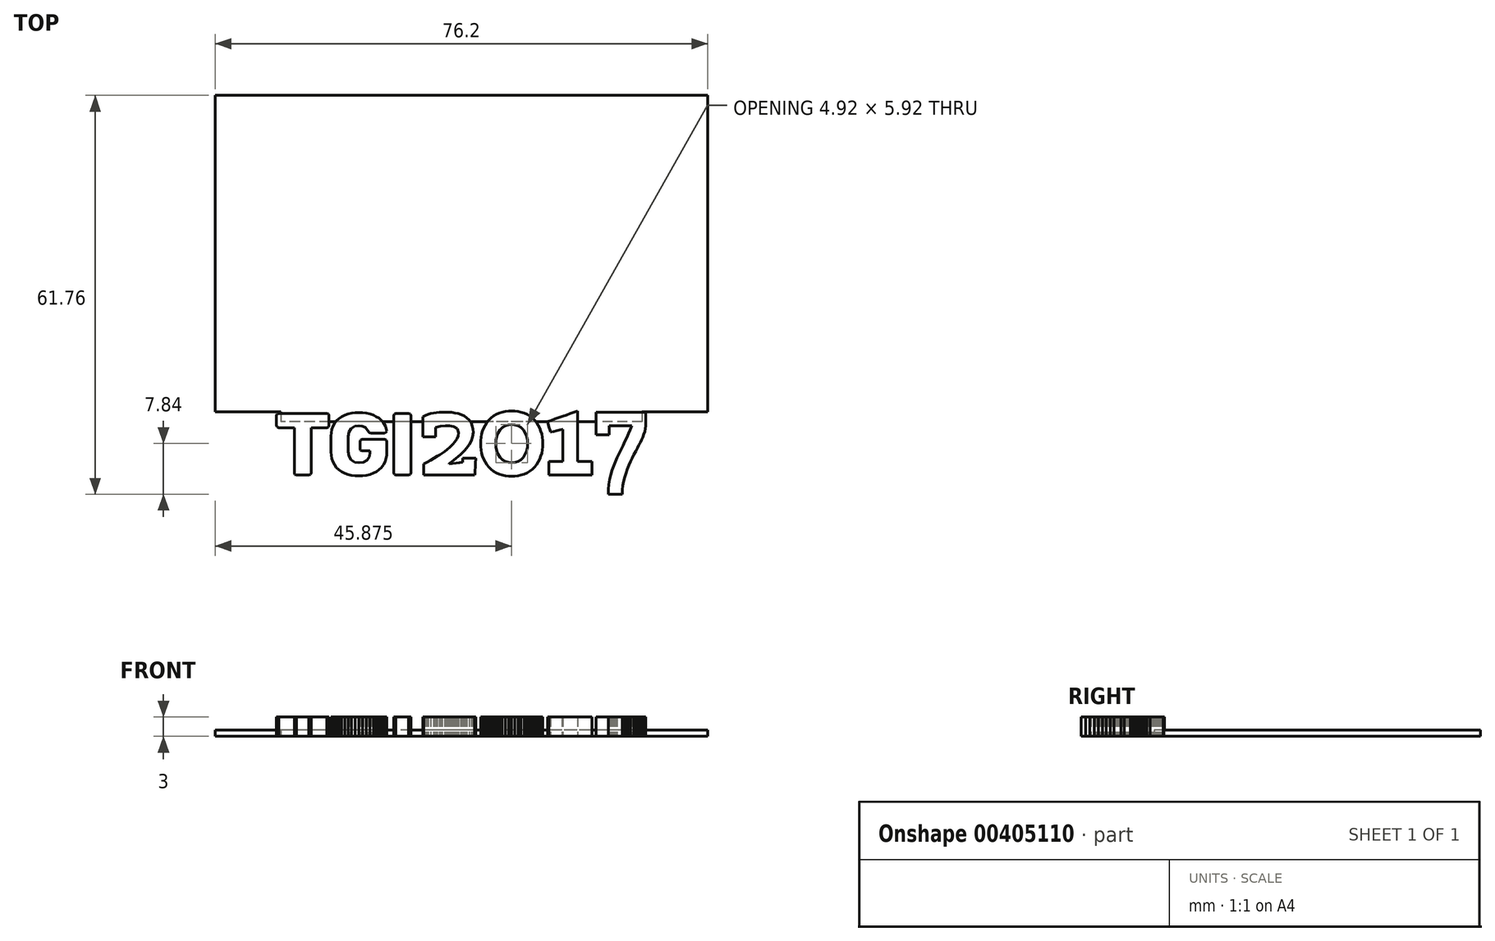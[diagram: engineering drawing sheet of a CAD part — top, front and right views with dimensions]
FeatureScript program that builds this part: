
annotation { "Feature Type Name" : "Feature", "Feature Type Description" : "" }
export const myFeature = defineFeature(function(context is Context, id is Id, definition is map)
    precondition{}
    {
        {
            var Q0;
            Q0=qCreatedBy(makeId("Top.planeOp"),FACE);
            var sketch = newSketch(context, id + "F0", { "sketchPlane" : qUnion([Q0])});
            skLineSegment(sketch, "E0.bottom", {"start": v(38.1, 24.5) * mm, "end": v(-38.1, 24.5) * mm});
            skLineSegment(sketch, "E0.top", {"start": v(38.1, -24.5) * mm, "end": v(-38.1, -24.5) * mm});
            skLineSegment(sketch, "E0.left", {"start": v(38.1, 24.5) * mm, "end": v(38.1, -24.5) * mm});
            skLineSegment(sketch, "E0.right", {"start": v(-38.1, 24.5) * mm, "end": v(-38.1, -24.5) * mm});
            skPoint(sketch, "E0.middle", {"position": v(0, 0) * mm});
            skPoint(sketch, "E1.middle", {"position": v(0, -24.5) * mm});
            skLineSegment(sketch, "E2.bottom", {"start": v(27.94, -23) * mm, "end": v(-27.94, -23) * mm});
            skLineSegment(sketch, "E2.top", {"start": v(27.94, -26) * mm, "end": v(-27.94, -26) * mm});
            skLineSegment(sketch, "E2.left", {"start": v(27.94, -23) * mm, "end": v(27.94, -26) * mm});
            skLineSegment(sketch, "E2.right", {"start": v(-27.94, -23) * mm, "end": v(-27.94, -26) * mm});
            skSolve(sketch);
        }
        {
            var Q0;
            Q0=makeQuery(id+"F0.imprint","IMPRINT",FACE,{"disambiguationData":[TD([[makeQuery(id+"F0.imprint","IMPRINT",EDGE,{"derivedFrom":sQuery(id+"F0.wireOp",EDGE,"E0.bottom")}),1.0]])]});
            var Q1;
            {var subQ5=sQuery(id+"F0.wireOp",EDGE,"E2.bottom");Q1=makeQuery(id+"F0.imprint","IMPRINT",FACE,{"disambiguationData":[TD([[makeQuery(id+"F0.imprint","IMPRINT",EDGE,{"derivedFrom":subQ5}),1.0]])]});}
            var Q2;
            {var subQ5=sQuery(id+"F0.wireOp",EDGE,"E2.top");Q2=makeQuery(id+"F0.imprint","IMPRINT",FACE,{"disambiguationData":[TD([[makeQuery(id+"F0.imprint","IMPRINT",EDGE,{"derivedFrom":subQ5}),-1.0]])]});}
            extrude(context, id + "F1", {"entities" : qUnion([Q0, Q1, Q2]), "depth" : 1 * mm});
        }
        {
            var Q0;
            Q0=qCreatedBy(makeId("Top.planeOp"),FACE);
            var sketch = newSketch(context, id + "F2", { "sketchPlane" : qUnion([Q0])});
            skLineSegment(sketch, "E3", {"start": v(-25.76, -34.2) * mm, "end": v(-25.86, -33.96) * mm});
            skLineSegment(sketch, "E4", {"start": v(-25.86, -33.96) * mm, "end": v(-25.86, -33.77) * mm});
            skLineSegment(sketch, "E5", {"start": v(-25.86, -33.77) * mm, "end": v(-25.86, -33.26) * mm});
            skLineSegment(sketch, "E6", {"start": v(-25.86, -33.26) * mm, "end": v(-25.86, -32.56) * mm});
            skLineSegment(sketch, "E7", {"start": v(-25.86, -32.56) * mm, "end": v(-25.86, -31.86) * mm});
            skLineSegment(sketch, "E8", {"start": v(-25.86, -31.86) * mm, "end": v(-25.86, -31.16) * mm});
            skLineSegment(sketch, "E9", {"start": v(-25.86, -31.16) * mm, "end": v(-25.86, -30.46) * mm});
            skLineSegment(sketch, "E10", {"start": v(-25.86, -30.46) * mm, "end": v(-25.86, -29.76) * mm});
            skLineSegment(sketch, "E11", {"start": v(-25.86, -29.76) * mm, "end": v(-25.86, -29.06) * mm});
            skLineSegment(sketch, "E12", {"start": v(-25.86, -29.06) * mm, "end": v(-25.86, -28.37) * mm});
            skLineSegment(sketch, "E13", {"start": v(-25.86, -28.37) * mm, "end": v(-25.86, -27.67) * mm});
            skLineSegment(sketch, "E14", {"start": v(-25.86, -27.67) * mm, "end": v(-25.86, -27.16) * mm});
            skLineSegment(sketch, "E15", {"start": v(-25.86, -27.16) * mm, "end": v(-25.86, -26.97) * mm});
            skLineSegment(sketch, "E16", {"start": v(-25.86, -26.97) * mm, "end": v(-26.03, -26.97) * mm});
            skLineSegment(sketch, "E17", {"start": v(-26.03, -26.97) * mm, "end": v(-26.46, -26.97) * mm});
            skLineSegment(sketch, "E18", {"start": v(-26.46, -26.97) * mm, "end": v(-27.06, -26.97) * mm});
            skLineSegment(sketch, "E19", {"start": v(-27.06, -26.97) * mm, "end": v(-27.66, -26.97) * mm});
            skLineSegment(sketch, "E20", {"start": v(-27.66, -26.97) * mm, "end": v(-28.1, -26.97) * mm});
            skLineSegment(sketch, "E21", {"start": v(-28.1, -26.97) * mm, "end": v(-28.26, -26.97) * mm});
            skLineSegment(sketch, "E22", {"start": v(-28.26, -26.97) * mm, "end": v(-28.52, -26.87) * mm});
            skLineSegment(sketch, "E23", {"start": v(-28.52, -26.87) * mm, "end": v(-28.62, -26.63) * mm});
            skLineSegment(sketch, "E24", {"start": v(-28.62, -26.63) * mm, "end": v(-28.62, -26.39) * mm});
            skLineSegment(sketch, "E25", {"start": v(-28.62, -26.39) * mm, "end": v(-28.62, -25.86) * mm});
            skLineSegment(sketch, "E26", {"start": v(-28.62, -25.86) * mm, "end": v(-28.62, -25.34) * mm});
            skLineSegment(sketch, "E27", {"start": v(-28.62, -25.34) * mm, "end": v(-28.62, -25.1) * mm});
            skLineSegment(sketch, "E28", {"start": v(-28.62, -25.1) * mm, "end": v(-28.52, -24.85) * mm});
            skLineSegment(sketch, "E29", {"start": v(-28.52, -24.85) * mm, "end": v(-28.26, -24.74) * mm});
            skLineSegment(sketch, "E30", {"start": v(-28.26, -24.74) * mm, "end": v(-27.65, -24.74) * mm});
            skLineSegment(sketch, "E31", {"start": v(-27.65, -24.74) * mm, "end": v(-27.03, -24.74) * mm});
            skLineSegment(sketch, "E32", {"start": v(-27.03, -24.74) * mm, "end": v(-26.41, -24.74) * mm});
            skLineSegment(sketch, "E33", {"start": v(-26.41, -24.74) * mm, "end": v(-25.8, -24.74) * mm});
            skLineSegment(sketch, "E34", {"start": v(-25.8, -24.74) * mm, "end": v(-25.18, -24.74) * mm});
            skLineSegment(sketch, "E35", {"start": v(-25.18, -24.74) * mm, "end": v(-24.56, -24.74) * mm});
            skLineSegment(sketch, "E36", {"start": v(-24.56, -24.74) * mm, "end": v(-23.94, -24.74) * mm});
            skLineSegment(sketch, "E37", {"start": v(-23.94, -24.74) * mm, "end": v(-23.32, -24.74) * mm});
            skLineSegment(sketch, "E38", {"start": v(-23.32, -24.74) * mm, "end": v(-22.7, -24.74) * mm});
            skLineSegment(sketch, "E39", {"start": v(-22.7, -24.74) * mm, "end": v(-22.09, -24.74) * mm});
            skLineSegment(sketch, "E40", {"start": v(-22.09, -24.74) * mm, "end": v(-21.47, -24.74) * mm});
            skLineSegment(sketch, "E41", {"start": v(-21.47, -24.74) * mm, "end": v(-20.85, -24.74) * mm});
            skLineSegment(sketch, "E42", {"start": v(-20.85, -24.74) * mm, "end": v(-20.6, -24.85) * mm});
            skLineSegment(sketch, "E43", {"start": v(-20.6, -24.85) * mm, "end": v(-20.5, -25.1) * mm});
            skLineSegment(sketch, "E44", {"start": v(-20.5, -25.1) * mm, "end": v(-20.5, -25.34) * mm});
            skLineSegment(sketch, "E45", {"start": v(-20.5, -25.34) * mm, "end": v(-20.5, -25.86) * mm});
            skLineSegment(sketch, "E46", {"start": v(-20.5, -25.86) * mm, "end": v(-20.5, -26.39) * mm});
            skLineSegment(sketch, "E47", {"start": v(-20.5, -26.39) * mm, "end": v(-20.5, -26.63) * mm});
            skLineSegment(sketch, "E48", {"start": v(-20.5, -26.63) * mm, "end": v(-20.6, -26.87) * mm});
            skLineSegment(sketch, "E49", {"start": v(-20.6, -26.87) * mm, "end": v(-20.85, -26.97) * mm});
            skLineSegment(sketch, "E50", {"start": v(-20.85, -26.97) * mm, "end": v(-21.02, -26.97) * mm});
            skLineSegment(sketch, "E51", {"start": v(-21.02, -26.97) * mm, "end": v(-21.45, -26.97) * mm});
            skLineSegment(sketch, "E52", {"start": v(-21.45, -26.97) * mm, "end": v(-22.05, -26.97) * mm});
            skLineSegment(sketch, "E53", {"start": v(-22.05, -26.97) * mm, "end": v(-22.65, -26.97) * mm});
            skLineSegment(sketch, "E54", {"start": v(-22.65, -26.97) * mm, "end": v(-23.08, -26.97) * mm});
            skLineSegment(sketch, "E55", {"start": v(-23.08, -26.97) * mm, "end": v(-23.25, -26.97) * mm});
            skLineSegment(sketch, "E56", {"start": v(-23.25, -26.97) * mm, "end": v(-23.25, -27.16) * mm});
            skLineSegment(sketch, "E57", {"start": v(-23.25, -27.16) * mm, "end": v(-23.25, -27.67) * mm});
            skLineSegment(sketch, "E58", {"start": v(-23.25, -27.67) * mm, "end": v(-23.25, -28.37) * mm});
            skLineSegment(sketch, "E59", {"start": v(-23.25, -28.37) * mm, "end": v(-23.25, -29.06) * mm});
            skLineSegment(sketch, "E60", {"start": v(-23.25, -29.06) * mm, "end": v(-23.25, -29.76) * mm});
            skLineSegment(sketch, "E61", {"start": v(-23.25, -29.76) * mm, "end": v(-23.25, -30.46) * mm});
            skLineSegment(sketch, "E62", {"start": v(-23.25, -30.46) * mm, "end": v(-23.25, -31.16) * mm});
            skLineSegment(sketch, "E63", {"start": v(-23.25, -31.16) * mm, "end": v(-23.25, -31.86) * mm});
            skLineSegment(sketch, "E64", {"start": v(-23.25, -31.86) * mm, "end": v(-23.25, -32.56) * mm});
            skLineSegment(sketch, "E65", {"start": v(-23.25, -32.56) * mm, "end": v(-23.25, -33.26) * mm});
            skLineSegment(sketch, "E66", {"start": v(-23.25, -33.26) * mm, "end": v(-23.25, -33.77) * mm});
            skLineSegment(sketch, "E67", {"start": v(-23.25, -33.77) * mm, "end": v(-23.25, -33.96) * mm});
            skLineSegment(sketch, "E68", {"start": v(-23.25, -33.96) * mm, "end": v(-23.36, -34.2) * mm});
            skLineSegment(sketch, "E69", {"start": v(-23.36, -34.2) * mm, "end": v(-23.6, -34.3) * mm});
            skLineSegment(sketch, "E70", {"start": v(-23.6, -34.3) * mm, "end": v(-24.08, -34.3) * mm});
            skLineSegment(sketch, "E71", {"start": v(-24.08, -34.3) * mm, "end": v(-24.56, -34.3) * mm});
            skLineSegment(sketch, "E72", {"start": v(-24.56, -34.3) * mm, "end": v(-25.03, -34.3) * mm});
            skLineSegment(sketch, "E73", {"start": v(-25.03, -34.3) * mm, "end": v(-25.5, -34.3) * mm});
            skLineSegment(sketch, "E74", {"start": v(-25.5, -34.3) * mm, "end": v(-25.76, -34.2) * mm});
            skLineSegment(sketch, "E75", {"start": v(-18.99, -33.47) * mm, "end": v(-19.35, -33.1) * mm});
            skLineSegment(sketch, "E76", {"start": v(-19.35, -33.1) * mm, "end": v(-19.65, -32.69) * mm});
            skLineSegment(sketch, "E77", {"start": v(-19.65, -32.69) * mm, "end": v(-19.87, -32.23) * mm});
            skLineSegment(sketch, "E78", {"start": v(-19.87, -32.23) * mm, "end": v(-20.03, -31.74) * mm});
            skLineSegment(sketch, "E79", {"start": v(-20.03, -31.74) * mm, "end": v(-20.13, -31.24) * mm});
            skLineSegment(sketch, "E80", {"start": v(-20.13, -31.24) * mm, "end": v(-20.17, -30.72) * mm});
            skLineSegment(sketch, "E81", {"start": v(-20.17, -30.72) * mm, "end": v(-20.19, -30.1) * mm});
            skLineSegment(sketch, "E82", {"start": v(-20.19, -30.1) * mm, "end": v(-20.19, -29.48) * mm});
            skLineSegment(sketch, "E83", {"start": v(-20.19, -29.48) * mm, "end": v(-20.19, -28.85) * mm});
            skLineSegment(sketch, "E84", {"start": v(-20.19, -28.85) * mm, "end": v(-20.17, -28.22) * mm});
            skLineSegment(sketch, "E85", {"start": v(-20.17, -28.22) * mm, "end": v(-20.13, -27.72) * mm});
            skLineSegment(sketch, "E86", {"start": v(-20.13, -27.72) * mm, "end": v(-20.04, -27.23) * mm});
            skLineSegment(sketch, "E87", {"start": v(-20.04, -27.23) * mm, "end": v(-19.87, -26.75) * mm});
            skLineSegment(sketch, "E88", {"start": v(-19.87, -26.75) * mm, "end": v(-19.64, -26.3) * mm});
            skLineSegment(sketch, "E89", {"start": v(-19.64, -26.3) * mm, "end": v(-19.34, -25.9) * mm});
            skLineSegment(sketch, "E90", {"start": v(-19.34, -25.9) * mm, "end": v(-18.98, -25.56) * mm});
            skLineSegment(sketch, "E91", {"start": v(-18.98, -25.56) * mm, "end": v(-18.53, -25.24) * mm});
            skLineSegment(sketch, "E92", {"start": v(-18.53, -25.24) * mm, "end": v(-18.04, -25) * mm});
            skLineSegment(sketch, "E93", {"start": v(-18.04, -25) * mm, "end": v(-17.52, -24.8) * mm});
            skLineSegment(sketch, "E94", {"start": v(-17.52, -24.8) * mm, "end": v(-16.98, -24.7) * mm});
            skLineSegment(sketch, "E95", {"start": v(-16.98, -24.7) * mm, "end": v(-16.44, -24.63) * mm});
            skLineSegment(sketch, "E96", {"start": v(-16.44, -24.63) * mm, "end": v(-15.89, -24.6) * mm});
            skLineSegment(sketch, "E97", {"start": v(-15.89, -24.6) * mm, "end": v(-15.3, -24.63) * mm});
            skLineSegment(sketch, "E98", {"start": v(-15.3, -24.63) * mm, "end": v(-14.72, -24.7) * mm});
            skLineSegment(sketch, "E99", {"start": v(-14.72, -24.7) * mm, "end": v(-14.15, -24.83) * mm});
            skLineSegment(sketch, "E100", {"start": v(-14.15, -24.83) * mm, "end": v(-13.6, -25.03) * mm});
            skLineSegment(sketch, "E101", {"start": v(-13.6, -25.03) * mm, "end": v(-13.18, -25.23) * mm});
            skLineSegment(sketch, "E102", {"start": v(-13.18, -25.23) * mm, "end": v(-12.79, -25.48) * mm});
            skLineSegment(sketch, "E103", {"start": v(-12.79, -25.48) * mm, "end": v(-12.43, -25.77) * mm});
            skLineSegment(sketch, "E104", {"start": v(-12.43, -25.77) * mm, "end": v(-12.11, -26.12) * mm});
            skLineSegment(sketch, "E105", {"start": v(-12.11, -26.12) * mm, "end": v(-11.74, -26.75) * mm});
            skLineSegment(sketch, "E106", {"start": v(-11.74, -26.75) * mm, "end": v(-11.57, -27.47) * mm});
            skLineSegment(sketch, "E107", {"start": v(-11.57, -27.47) * mm, "end": v(-11.66, -27.69) * mm});
            skLineSegment(sketch, "E108", {"start": v(-11.66, -27.69) * mm, "end": v(-11.87, -27.77) * mm});
            skLineSegment(sketch, "E109", {"start": v(-11.87, -27.77) * mm, "end": v(-12.4, -27.77) * mm});
            skLineSegment(sketch, "E110", {"start": v(-12.4, -27.77) * mm, "end": v(-12.93, -27.77) * mm});
            skLineSegment(sketch, "E111", {"start": v(-12.93, -27.77) * mm, "end": v(-13.46, -27.77) * mm});
            skLineSegment(sketch, "E112", {"start": v(-13.46, -27.77) * mm, "end": v(-14, -27.77) * mm});
            skLineSegment(sketch, "E113", {"start": v(-14, -27.77) * mm, "end": v(-14.2, -27.73) * mm});
            skLineSegment(sketch, "E114", {"start": v(-14.2, -27.73) * mm, "end": v(-14.34, -27.58) * mm});
            skLineSegment(sketch, "E115", {"start": v(-14.34, -27.58) * mm, "end": v(-14.87, -26.93) * mm});
            skLineSegment(sketch, "E116", {"start": v(-14.87, -26.93) * mm, "end": v(-15.36, -26.7) * mm});
            skLineSegment(sketch, "E117", {"start": v(-15.36, -26.7) * mm, "end": v(-15.89, -26.65) * mm});
            skLineSegment(sketch, "E118", {"start": v(-15.89, -26.65) * mm, "end": v(-16.54, -26.74) * mm});
            skLineSegment(sketch, "E119", {"start": v(-16.54, -26.74) * mm, "end": v(-17.1, -27.08) * mm});
            skLineSegment(sketch, "E120", {"start": v(-17.1, -27.08) * mm, "end": v(-17.43, -27.64) * mm});
            skLineSegment(sketch, "E121", {"start": v(-17.43, -27.64) * mm, "end": v(-17.53, -28.3) * mm});
            skLineSegment(sketch, "E122", {"start": v(-17.53, -28.3) * mm, "end": v(-17.54, -28.88) * mm});
            skLineSegment(sketch, "E123", {"start": v(-17.54, -28.88) * mm, "end": v(-17.54, -29.47) * mm});
            skLineSegment(sketch, "E124", {"start": v(-17.54, -29.47) * mm, "end": v(-17.54, -30.06) * mm});
            skLineSegment(sketch, "E125", {"start": v(-17.54, -30.06) * mm, "end": v(-17.53, -30.65) * mm});
            skLineSegment(sketch, "E126", {"start": v(-17.53, -30.65) * mm, "end": v(-17.43, -31.33) * mm});
            skLineSegment(sketch, "E127", {"start": v(-17.43, -31.33) * mm, "end": v(-17.1, -31.93) * mm});
            skLineSegment(sketch, "E128", {"start": v(-17.1, -31.93) * mm, "end": v(-16.54, -32.3) * mm});
            skLineSegment(sketch, "E129", {"start": v(-16.54, -32.3) * mm, "end": v(-15.86, -32.39) * mm});
            skLineSegment(sketch, "E130", {"start": v(-15.86, -32.39) * mm, "end": v(-15.2, -32.3) * mm});
            skLineSegment(sketch, "E131", {"start": v(-15.2, -32.3) * mm, "end": v(-14.6, -32) * mm});
            skLineSegment(sketch, "E132", {"start": v(-14.6, -32) * mm, "end": v(-14.24, -31.45) * mm});
            skLineSegment(sketch, "E133", {"start": v(-14.24, -31.45) * mm, "end": v(-14.14, -30.8) * mm});
            skLineSegment(sketch, "E134", {"start": v(-14.14, -30.8) * mm, "end": v(-14.14, -30.67) * mm});
            skLineSegment(sketch, "E135", {"start": v(-14.14, -30.67) * mm, "end": v(-14.14, -30.54) * mm});
            skLineSegment(sketch, "E136", {"start": v(-14.14, -30.54) * mm, "end": v(-14.33, -30.54) * mm});
            skLineSegment(sketch, "E137", {"start": v(-14.33, -30.54) * mm, "end": v(-14.75, -30.54) * mm});
            skLineSegment(sketch, "E138", {"start": v(-14.75, -30.54) * mm, "end": v(-15.17, -30.54) * mm});
            skLineSegment(sketch, "E139", {"start": v(-15.17, -30.54) * mm, "end": v(-15.36, -30.54) * mm});
            skLineSegment(sketch, "E140", {"start": v(-15.36, -30.54) * mm, "end": v(-15.6, -30.44) * mm});
            skLineSegment(sketch, "E141", {"start": v(-15.6, -30.44) * mm, "end": v(-15.71, -30.2) * mm});
            skLineSegment(sketch, "E142", {"start": v(-15.71, -30.2) * mm, "end": v(-15.71, -30.02) * mm});
            skLineSegment(sketch, "E143", {"start": v(-15.71, -30.02) * mm, "end": v(-15.71, -29.66) * mm});
            skLineSegment(sketch, "E144", {"start": v(-15.71, -29.66) * mm, "end": v(-15.71, -29.3) * mm});
            skLineSegment(sketch, "E145", {"start": v(-15.71, -29.3) * mm, "end": v(-15.71, -29.13) * mm});
            skLineSegment(sketch, "E146", {"start": v(-15.71, -29.13) * mm, "end": v(-15.6, -28.87) * mm});
            skLineSegment(sketch, "E147", {"start": v(-15.6, -28.87) * mm, "end": v(-15.36, -28.77) * mm});
            skLineSegment(sketch, "E148", {"start": v(-15.36, -28.77) * mm, "end": v(-14.78, -28.77) * mm});
            skLineSegment(sketch, "E149", {"start": v(-14.78, -28.77) * mm, "end": v(-14.2, -28.77) * mm});
            skLineSegment(sketch, "E150", {"start": v(-14.2, -28.77) * mm, "end": v(-13.62, -28.77) * mm});
            skLineSegment(sketch, "E151", {"start": v(-13.62, -28.77) * mm, "end": v(-13.04, -28.77) * mm});
            skLineSegment(sketch, "E152", {"start": v(-13.04, -28.77) * mm, "end": v(-12.47, -28.77) * mm});
            skLineSegment(sketch, "E153", {"start": v(-12.47, -28.77) * mm, "end": v(-11.89, -28.77) * mm});
            skLineSegment(sketch, "E154", {"start": v(-11.89, -28.77) * mm, "end": v(-11.64, -28.87) * mm});
            skLineSegment(sketch, "E155", {"start": v(-11.64, -28.87) * mm, "end": v(-11.53, -29.13) * mm});
            skLineSegment(sketch, "E156", {"start": v(-11.53, -29.13) * mm, "end": v(-11.53, -29.37) * mm});
            skLineSegment(sketch, "E157", {"start": v(-11.53, -29.37) * mm, "end": v(-11.53, -29.92) * mm});
            skLineSegment(sketch, "E158", {"start": v(-11.53, -29.92) * mm, "end": v(-11.53, -30.46) * mm});
            skLineSegment(sketch, "E159", {"start": v(-11.53, -30.46) * mm, "end": v(-11.53, -30.7) * mm});
            skLineSegment(sketch, "E160", {"start": v(-11.53, -30.7) * mm, "end": v(-11.56, -31.23) * mm});
            skLineSegment(sketch, "E161", {"start": v(-11.56, -31.23) * mm, "end": v(-11.66, -31.75) * mm});
            skLineSegment(sketch, "E162", {"start": v(-11.66, -31.75) * mm, "end": v(-11.83, -32.25) * mm});
            skLineSegment(sketch, "E163", {"start": v(-11.83, -32.25) * mm, "end": v(-12.07, -32.7) * mm});
            skLineSegment(sketch, "E164", {"start": v(-12.07, -32.7) * mm, "end": v(-12.38, -33.11) * mm});
            skLineSegment(sketch, "E165", {"start": v(-12.38, -33.11) * mm, "end": v(-12.74, -33.46) * mm});
            skLineSegment(sketch, "E166", {"start": v(-12.74, -33.46) * mm, "end": v(-13.15, -33.76) * mm});
            skLineSegment(sketch, "E167", {"start": v(-13.15, -33.76) * mm, "end": v(-13.6, -34) * mm});
            skLineSegment(sketch, "E168", {"start": v(-13.6, -34) * mm, "end": v(-14.14, -34.2) * mm});
            skLineSegment(sketch, "E169", {"start": v(-14.14, -34.2) * mm, "end": v(-14.72, -34.34) * mm});
            skLineSegment(sketch, "E170", {"start": v(-14.72, -34.34) * mm, "end": v(-15.3, -34.41) * mm});
            skLineSegment(sketch, "E171", {"start": v(-15.3, -34.41) * mm, "end": v(-15.89, -34.44) * mm});
            skLineSegment(sketch, "E172", {"start": v(-15.89, -34.44) * mm, "end": v(-16.44, -34.42) * mm});
            skLineSegment(sketch, "E173", {"start": v(-16.44, -34.42) * mm, "end": v(-16.99, -34.35) * mm});
            skLineSegment(sketch, "E174", {"start": v(-16.99, -34.35) * mm, "end": v(-17.53, -34.23) * mm});
            skLineSegment(sketch, "E175", {"start": v(-17.53, -34.23) * mm, "end": v(-18.05, -34.05) * mm});
            skLineSegment(sketch, "E176", {"start": v(-18.05, -34.05) * mm, "end": v(-18.54, -33.8) * mm});
            skLineSegment(sketch, "E177", {"start": v(-18.54, -33.8) * mm, "end": v(-18.99, -33.47) * mm});
            skLineSegment(sketch, "E178", {"start": v(-10.37, -34.2) * mm, "end": v(-10.47, -33.96) * mm});
            skLineSegment(sketch, "E179", {"start": v(-10.47, -33.96) * mm, "end": v(-10.47, -33.8) * mm});
            skLineSegment(sketch, "E180", {"start": v(-10.47, -33.8) * mm, "end": v(-10.47, -33.32) * mm});
            skLineSegment(sketch, "E181", {"start": v(-10.47, -33.32) * mm, "end": v(-10.47, -32.7) * mm});
            skLineSegment(sketch, "E182", {"start": v(-10.47, -32.7) * mm, "end": v(-10.47, -32.06) * mm});
            skLineSegment(sketch, "E183", {"start": v(-10.47, -32.06) * mm, "end": v(-10.47, -31.42) * mm});
            skLineSegment(sketch, "E184", {"start": v(-10.47, -31.42) * mm, "end": v(-10.47, -30.79) * mm});
            skLineSegment(sketch, "E185", {"start": v(-10.47, -30.79) * mm, "end": v(-10.47, -30.15) * mm});
            skLineSegment(sketch, "E186", {"start": v(-10.47, -30.15) * mm, "end": v(-10.47, -29.52) * mm});
            skLineSegment(sketch, "E187", {"start": v(-10.47, -29.52) * mm, "end": v(-10.47, -28.89) * mm});
            skLineSegment(sketch, "E188", {"start": v(-10.47, -28.89) * mm, "end": v(-10.47, -28.25) * mm});
            skLineSegment(sketch, "E189", {"start": v(-10.47, -28.25) * mm, "end": v(-10.47, -27.62) * mm});
            skLineSegment(sketch, "E190", {"start": v(-10.47, -27.62) * mm, "end": v(-10.47, -26.99) * mm});
            skLineSegment(sketch, "E191", {"start": v(-10.47, -26.99) * mm, "end": v(-10.47, -26.35) * mm});
            skLineSegment(sketch, "E192", {"start": v(-10.47, -26.35) * mm, "end": v(-10.47, -25.72) * mm});
            skLineSegment(sketch, "E193", {"start": v(-10.47, -25.72) * mm, "end": v(-10.47, -25.25) * mm});
            skLineSegment(sketch, "E194", {"start": v(-10.47, -25.25) * mm, "end": v(-10.47, -25.09) * mm});
            skLineSegment(sketch, "E195", {"start": v(-10.47, -25.09) * mm, "end": v(-10.37, -24.84) * mm});
            skLineSegment(sketch, "E196", {"start": v(-10.37, -24.84) * mm, "end": v(-10.13, -24.74) * mm});
            skLineSegment(sketch, "E197", {"start": v(-10.13, -24.74) * mm, "end": v(-9.64, -24.74) * mm});
            skLineSegment(sketch, "E198", {"start": v(-9.64, -24.74) * mm, "end": v(-9.15, -24.74) * mm});
            skLineSegment(sketch, "E199", {"start": v(-9.15, -24.74) * mm, "end": v(-8.67, -24.74) * mm});
            skLineSegment(sketch, "E200", {"start": v(-8.67, -24.74) * mm, "end": v(-8.18, -24.74) * mm});
            skLineSegment(sketch, "E201", {"start": v(-8.18, -24.74) * mm, "end": v(-7.93, -24.84) * mm});
            skLineSegment(sketch, "E202", {"start": v(-7.93, -24.84) * mm, "end": v(-7.84, -25.09) * mm});
            skLineSegment(sketch, "E203", {"start": v(-7.84, -25.09) * mm, "end": v(-7.84, -25.25) * mm});
            skLineSegment(sketch, "E204", {"start": v(-7.84, -25.25) * mm, "end": v(-7.84, -25.72) * mm});
            skLineSegment(sketch, "E205", {"start": v(-7.84, -25.72) * mm, "end": v(-7.84, -26.35) * mm});
            skLineSegment(sketch, "E206", {"start": v(-7.84, -26.35) * mm, "end": v(-7.84, -26.99) * mm});
            skLineSegment(sketch, "E207", {"start": v(-7.84, -26.99) * mm, "end": v(-7.84, -27.62) * mm});
            skLineSegment(sketch, "E208", {"start": v(-7.84, -27.62) * mm, "end": v(-7.84, -28.25) * mm});
            skLineSegment(sketch, "E209", {"start": v(-7.84, -28.25) * mm, "end": v(-7.84, -28.89) * mm});
            skLineSegment(sketch, "E210", {"start": v(-7.84, -28.89) * mm, "end": v(-7.84, -29.52) * mm});
            skLineSegment(sketch, "E211", {"start": v(-7.84, -29.52) * mm, "end": v(-7.84, -30.15) * mm});
            skLineSegment(sketch, "E212", {"start": v(-7.84, -30.15) * mm, "end": v(-7.84, -30.79) * mm});
            skLineSegment(sketch, "E213", {"start": v(-7.84, -30.79) * mm, "end": v(-7.84, -31.42) * mm});
            skLineSegment(sketch, "E214", {"start": v(-7.84, -31.42) * mm, "end": v(-7.84, -32.06) * mm});
            skLineSegment(sketch, "E215", {"start": v(-7.84, -32.06) * mm, "end": v(-7.84, -32.7) * mm});
            skLineSegment(sketch, "E216", {"start": v(-7.84, -32.7) * mm, "end": v(-7.84, -33.32) * mm});
            skLineSegment(sketch, "E217", {"start": v(-7.84, -33.32) * mm, "end": v(-7.84, -33.8) * mm});
            skLineSegment(sketch, "E218", {"start": v(-7.84, -33.8) * mm, "end": v(-7.84, -33.96) * mm});
            skLineSegment(sketch, "E219", {"start": v(-7.84, -33.96) * mm, "end": v(-7.93, -34.2) * mm});
            skLineSegment(sketch, "E220", {"start": v(-7.93, -34.2) * mm, "end": v(-8.18, -34.3) * mm});
            skLineSegment(sketch, "E221", {"start": v(-8.18, -34.3) * mm, "end": v(-8.67, -34.3) * mm});
            skLineSegment(sketch, "E222", {"start": v(-8.67, -34.3) * mm, "end": v(-9.15, -34.3) * mm});
            skLineSegment(sketch, "E223", {"start": v(-9.15, -34.3) * mm, "end": v(-9.64, -34.3) * mm});
            skLineSegment(sketch, "E224", {"start": v(-9.64, -34.3) * mm, "end": v(-10.13, -34.3) * mm});
            skLineSegment(sketch, "E225", {"start": v(-10.13, -34.3) * mm, "end": v(-10.37, -34.2) * mm});
            skLineSegment(sketch, "E226", {"start": v(-5.85, -34.3) * mm, "end": v(-5.85, -34.03) * mm});
            skLineSegment(sketch, "E227", {"start": v(-5.85, -34.03) * mm, "end": v(-5.85, -33.43) * mm});
            skLineSegment(sketch, "E228", {"start": v(-5.85, -33.43) * mm, "end": v(-5.85, -32.83) * mm});
            skLineSegment(sketch, "E229", {"start": v(-5.85, -32.83) * mm, "end": v(-5.85, -32.56) * mm});
            skLineSegment(sketch, "E230", {"start": v(-5.85, -32.56) * mm, "end": v(-5.32, -32.28) * mm});
            skLineSegment(sketch, "E231", {"start": v(-5.32, -32.28) * mm, "end": v(-4.79, -32) * mm});
            skLineSegment(sketch, "E232", {"start": v(-4.79, -32) * mm, "end": v(-4.27, -31.7) * mm});
            skLineSegment(sketch, "E233", {"start": v(-4.27, -31.7) * mm, "end": v(-3.75, -31.38) * mm});
            skLineSegment(sketch, "E234", {"start": v(-3.75, -31.38) * mm, "end": v(-3.37, -31.14) * mm});
            skLineSegment(sketch, "E235", {"start": v(-3.37, -31.14) * mm, "end": v(-2.98, -30.89) * mm});
            skLineSegment(sketch, "E236", {"start": v(-2.98, -30.89) * mm, "end": v(-2.6, -30.63) * mm});
            skLineSegment(sketch, "E237", {"start": v(-2.6, -30.63) * mm, "end": v(-2.25, -30.35) * mm});
            skLineSegment(sketch, "E238", {"start": v(-2.25, -30.35) * mm, "end": v(-1.8, -29.96) * mm});
            skLineSegment(sketch, "E239", {"start": v(-1.8, -29.96) * mm, "end": v(-1.36, -29.54) * mm});
            skLineSegment(sketch, "E240", {"start": v(-1.36, -29.54) * mm, "end": v(-1, -29.15) * mm});
            skLineSegment(sketch, "E241", {"start": v(-1, -29.15) * mm, "end": v(-0.7, -28.72) * mm});
            skLineSegment(sketch, "E242", {"start": v(-0.7, -28.72) * mm, "end": v(-0.5, -28.23) * mm});
            skLineSegment(sketch, "E243", {"start": v(-0.5, -28.23) * mm, "end": v(-0.43, -27.71) * mm});
            skLineSegment(sketch, "E244", {"start": v(-0.43, -27.71) * mm, "end": v(-0.65, -27.12) * mm});
            skLineSegment(sketch, "E245", {"start": v(-0.65, -27.12) * mm, "end": v(-1.2, -26.8) * mm});
            skLineSegment(sketch, "E246", {"start": v(-1.2, -26.8) * mm, "end": v(-1.83, -26.66) * mm});
            skLineSegment(sketch, "E247", {"start": v(-1.83, -26.66) * mm, "end": v(-2.47, -26.63) * mm});
            skLineSegment(sketch, "E248", {"start": v(-2.47, -26.63) * mm, "end": v(-3.24, -26.7) * mm});
            skLineSegment(sketch, "E249", {"start": v(-3.24, -26.7) * mm, "end": v(-3.97, -26.93) * mm});
            skLineSegment(sketch, "E250", {"start": v(-3.97, -26.93) * mm, "end": v(-3.97, -27.15) * mm});
            skLineSegment(sketch, "E251", {"start": v(-3.97, -27.15) * mm, "end": v(-3.97, -27.65) * mm});
            skLineSegment(sketch, "E252", {"start": v(-3.97, -27.65) * mm, "end": v(-3.97, -28.15) * mm});
            skLineSegment(sketch, "E253", {"start": v(-3.97, -28.15) * mm, "end": v(-3.97, -28.37) * mm});
            skLineSegment(sketch, "E254", {"start": v(-3.97, -28.37) * mm, "end": v(-4.47, -28.37) * mm});
            skLineSegment(sketch, "E255", {"start": v(-4.47, -28.37) * mm, "end": v(-4.97, -28.37) * mm});
            skLineSegment(sketch, "E256", {"start": v(-4.97, -28.37) * mm, "end": v(-5.47, -28.37) * mm});
            skLineSegment(sketch, "E257", {"start": v(-5.47, -28.37) * mm, "end": v(-5.97, -28.37) * mm});
            skLineSegment(sketch, "E258", {"start": v(-5.97, -28.37) * mm, "end": v(-5.97, -28.15) * mm});
            skLineSegment(sketch, "E259", {"start": v(-5.97, -28.15) * mm, "end": v(-5.97, -27.6) * mm});
            skLineSegment(sketch, "E260", {"start": v(-5.97, -27.6) * mm, "end": v(-5.97, -26.81) * mm});
            skLineSegment(sketch, "E261", {"start": v(-5.97, -26.81) * mm, "end": v(-5.97, -26.03) * mm});
            skLineSegment(sketch, "E262", {"start": v(-5.97, -26.03) * mm, "end": v(-5.97, -25.48) * mm});
            skLineSegment(sketch, "E263", {"start": v(-5.97, -25.48) * mm, "end": v(-5.97, -25.25) * mm});
            skLineSegment(sketch, "E264", {"start": v(-5.97, -25.25) * mm, "end": v(-5.57, -25.06) * mm});
            skLineSegment(sketch, "E265", {"start": v(-5.57, -25.06) * mm, "end": v(-5.16, -24.9) * mm});
            skLineSegment(sketch, "E266", {"start": v(-5.16, -24.9) * mm, "end": v(-4.73, -24.78) * mm});
            skLineSegment(sketch, "E267", {"start": v(-4.73, -24.78) * mm, "end": v(-4.3, -24.69) * mm});
            skLineSegment(sketch, "E268", {"start": v(-4.3, -24.69) * mm, "end": v(-3.85, -24.62) * mm});
            skLineSegment(sketch, "E269", {"start": v(-3.85, -24.62) * mm, "end": v(-3.41, -24.57) * mm});
            skLineSegment(sketch, "E270", {"start": v(-3.41, -24.57) * mm, "end": v(-2.97, -24.55) * mm});
            skLineSegment(sketch, "E271", {"start": v(-2.97, -24.55) * mm, "end": v(-2.52, -24.54) * mm});
            skLineSegment(sketch, "E272", {"start": v(-2.52, -24.54) * mm, "end": v(-2.02, -24.55) * mm});
            skLineSegment(sketch, "E273", {"start": v(-2.02, -24.55) * mm, "end": v(-1.5, -24.59) * mm});
            skLineSegment(sketch, "E274", {"start": v(-1.5, -24.59) * mm, "end": v(-1, -24.66) * mm});
            skLineSegment(sketch, "E275", {"start": v(-1, -24.66) * mm, "end": v(-0.5, -24.77) * mm});
            skLineSegment(sketch, "E276", {"start": v(-0.5, -24.77) * mm, "end": v(-0.02, -24.93) * mm});
            skLineSegment(sketch, "E277", {"start": v(-0.02, -24.93) * mm, "end": v(0.44, -25.14) * mm});
            skLineSegment(sketch, "E278", {"start": v(0.44, -25.14) * mm, "end": v(0.86, -25.43) * mm});
            skLineSegment(sketch, "E279", {"start": v(0.86, -25.43) * mm, "end": v(1.22, -25.79) * mm});
            skLineSegment(sketch, "E280", {"start": v(1.22, -25.79) * mm, "end": v(1.5, -26.22) * mm});
            skLineSegment(sketch, "E281", {"start": v(1.5, -26.22) * mm, "end": v(1.68, -26.69) * mm});
            skLineSegment(sketch, "E282", {"start": v(1.68, -26.69) * mm, "end": v(1.78, -27.19) * mm});
            skLineSegment(sketch, "E283", {"start": v(1.78, -27.19) * mm, "end": v(1.81, -27.7) * mm});
            skLineSegment(sketch, "E284", {"start": v(1.81, -27.7) * mm, "end": v(1.73, -28.37) * mm});
            skLineSegment(sketch, "E285", {"start": v(1.73, -28.37) * mm, "end": v(1.51, -29) * mm});
            skLineSegment(sketch, "E286", {"start": v(1.51, -29) * mm, "end": v(1.18, -29.6) * mm});
            skLineSegment(sketch, "E287", {"start": v(1.18, -29.6) * mm, "end": v(0.78, -30.15) * mm});
            skLineSegment(sketch, "E288", {"start": v(0.78, -30.15) * mm, "end": v(0.48, -30.49) * mm});
            skLineSegment(sketch, "E289", {"start": v(0.48, -30.49) * mm, "end": v(0.18, -30.81) * mm});
            skLineSegment(sketch, "E290", {"start": v(0.18, -30.81) * mm, "end": v(-0.15, -31.12) * mm});
            skLineSegment(sketch, "E291", {"start": v(-0.15, -31.12) * mm, "end": v(-0.48, -31.42) * mm});
            skLineSegment(sketch, "E292", {"start": v(-0.48, -31.42) * mm, "end": v(-0.82, -31.7) * mm});
            skLineSegment(sketch, "E293", {"start": v(-0.82, -31.7) * mm, "end": v(-1.18, -31.98) * mm});
            skLineSegment(sketch, "E294", {"start": v(-1.18, -31.98) * mm, "end": v(-1.54, -32.24) * mm});
            skLineSegment(sketch, "E295", {"start": v(-1.54, -32.24) * mm, "end": v(-1.91, -32.49) * mm});
            skLineSegment(sketch, "E296", {"start": v(-1.91, -32.49) * mm, "end": v(-1.88, -32.54) * mm});
            skLineSegment(sketch, "E297", {"start": v(-1.88, -32.54) * mm, "end": v(-1.73, -32.52) * mm});
            skLineSegment(sketch, "E298", {"start": v(-1.73, -32.52) * mm, "end": v(-1.36, -32.48) * mm});
            skLineSegment(sketch, "E299", {"start": v(-1.36, -32.48) * mm, "end": v(-0.85, -32.42) * mm});
            skLineSegment(sketch, "E300", {"start": v(-0.85, -32.42) * mm, "end": v(-0.34, -32.36) * mm});
            skLineSegment(sketch, "E301", {"start": v(-0.34, -32.36) * mm, "end": v(0.03, -32.31) * mm});
            skLineSegment(sketch, "E302", {"start": v(0.03, -32.31) * mm, "end": v(0.18, -32.3) * mm});
            skLineSegment(sketch, "E303", {"start": v(0.18, -32.3) * mm, "end": v(0.2, -31.99) * mm});
            skLineSegment(sketch, "E304", {"start": v(0.2, -31.99) * mm, "end": v(0.21, -31.68) * mm});
            skLineSegment(sketch, "E305", {"start": v(0.21, -31.68) * mm, "end": v(0.71, -31.68) * mm});
            skLineSegment(sketch, "E306", {"start": v(0.71, -31.68) * mm, "end": v(1.21, -31.68) * mm});
            skLineSegment(sketch, "E307", {"start": v(1.21, -31.68) * mm, "end": v(1.72, -31.68) * mm});
            skLineSegment(sketch, "E308", {"start": v(1.72, -31.68) * mm, "end": v(2.22, -31.68) * mm});
            skLineSegment(sketch, "E309", {"start": v(2.22, -31.68) * mm, "end": v(2.2, -31.87) * mm});
            skLineSegment(sketch, "E310", {"start": v(2.2, -31.87) * mm, "end": v(2.18, -32.34) * mm});
            skLineSegment(sketch, "E311", {"start": v(2.18, -32.34) * mm, "end": v(2.14, -33) * mm});
            skLineSegment(sketch, "E312", {"start": v(2.14, -33) * mm, "end": v(2.1, -33.65) * mm});
            skLineSegment(sketch, "E313", {"start": v(2.1, -33.65) * mm, "end": v(2.07, -34.11) * mm});
            skLineSegment(sketch, "E314", {"start": v(2.07, -34.11) * mm, "end": v(2.06, -34.3) * mm});
            skLineSegment(sketch, "E315", {"start": v(2.06, -34.3) * mm, "end": v(1.88, -34.3) * mm});
            skLineSegment(sketch, "E316", {"start": v(1.88, -34.3) * mm, "end": v(1.4, -34.3) * mm});
            skLineSegment(sketch, "E317", {"start": v(1.4, -34.3) * mm, "end": v(0.74, -34.3) * mm});
            skLineSegment(sketch, "E318", {"start": v(0.74, -34.3) * mm, "end": v(0.08, -34.3) * mm});
            skLineSegment(sketch, "E319", {"start": v(0.08, -34.3) * mm, "end": v(-0.58, -34.3) * mm});
            skLineSegment(sketch, "E320", {"start": v(-0.58, -34.3) * mm, "end": v(-1.24, -34.3) * mm});
            skLineSegment(sketch, "E321", {"start": v(-1.24, -34.3) * mm, "end": v(-1.9, -34.3) * mm});
            skLineSegment(sketch, "E322", {"start": v(-1.9, -34.3) * mm, "end": v(-2.56, -34.3) * mm});
            skLineSegment(sketch, "E323", {"start": v(-2.56, -34.3) * mm, "end": v(-3.22, -34.3) * mm});
            skLineSegment(sketch, "E324", {"start": v(-3.22, -34.3) * mm, "end": v(-3.87, -34.3) * mm});
            skLineSegment(sketch, "E325", {"start": v(-3.87, -34.3) * mm, "end": v(-4.53, -34.3) * mm});
            skLineSegment(sketch, "E326", {"start": v(-4.53, -34.3) * mm, "end": v(-5.2, -34.3) * mm});
            skLineSegment(sketch, "E327", {"start": v(-5.2, -34.3) * mm, "end": v(-5.68, -34.3) * mm});
            skLineSegment(sketch, "E328", {"start": v(-5.68, -34.3) * mm, "end": v(-5.85, -34.3) * mm});
            skLineSegment(sketch, "E329", {"start": v(5.32, -29.42) * mm, "end": v(5.35, -29.99) * mm});
            skLineSegment(sketch, "E330", {"start": v(5.35, -29.99) * mm, "end": v(5.47, -30.54) * mm});
            skLineSegment(sketch, "E331", {"start": v(5.47, -30.54) * mm, "end": v(5.68, -31.07) * mm});
            skLineSegment(sketch, "E332", {"start": v(5.68, -31.07) * mm, "end": v(5.99, -31.55) * mm});
            skLineSegment(sketch, "E333", {"start": v(5.99, -31.55) * mm, "end": v(6.35, -31.9) * mm});
            skLineSegment(sketch, "E334", {"start": v(6.35, -31.9) * mm, "end": v(6.78, -32.18) * mm});
            skLineSegment(sketch, "E335", {"start": v(6.78, -32.18) * mm, "end": v(7.27, -32.34) * mm});
            skLineSegment(sketch, "E336", {"start": v(7.27, -32.34) * mm, "end": v(7.78, -32.38) * mm});
            skLineSegment(sketch, "E337", {"start": v(7.78, -32.38) * mm, "end": v(8.3, -32.34) * mm});
            skLineSegment(sketch, "E338", {"start": v(8.3, -32.34) * mm, "end": v(8.78, -32.18) * mm});
            skLineSegment(sketch, "E339", {"start": v(8.78, -32.18) * mm, "end": v(9.21, -31.9) * mm});
            skLineSegment(sketch, "E340", {"start": v(9.21, -31.9) * mm, "end": v(9.57, -31.55) * mm});
            skLineSegment(sketch, "E341", {"start": v(9.57, -31.55) * mm, "end": v(9.88, -31.07) * mm});
            skLineSegment(sketch, "E342", {"start": v(9.88, -31.07) * mm, "end": v(10.08, -30.54) * mm});
            skLineSegment(sketch, "E343", {"start": v(10.08, -30.54) * mm, "end": v(10.2, -29.99) * mm});
            skLineSegment(sketch, "E344", {"start": v(10.2, -29.99) * mm, "end": v(10.23, -29.42) * mm});
            skLineSegment(sketch, "E345", {"start": v(10.23, -29.42) * mm, "end": v(10.2, -28.85) * mm});
            skLineSegment(sketch, "E346", {"start": v(10.2, -28.85) * mm, "end": v(10.08, -28.3) * mm});
            skLineSegment(sketch, "E347", {"start": v(10.08, -28.3) * mm, "end": v(9.87, -27.77) * mm});
            skLineSegment(sketch, "E348", {"start": v(9.87, -27.77) * mm, "end": v(9.56, -27.3) * mm});
            skLineSegment(sketch, "E349", {"start": v(9.56, -27.3) * mm, "end": v(9.2, -26.93) * mm});
            skLineSegment(sketch, "E350", {"start": v(9.2, -26.93) * mm, "end": v(8.77, -26.66) * mm});
            skLineSegment(sketch, "E351", {"start": v(8.77, -26.66) * mm, "end": v(8.28, -26.5) * mm});
            skLineSegment(sketch, "E352", {"start": v(8.28, -26.5) * mm, "end": v(7.77, -26.46) * mm});
            skLineSegment(sketch, "E353", {"start": v(7.77, -26.46) * mm, "end": v(7.26, -26.5) * mm});
            skLineSegment(sketch, "E354", {"start": v(7.26, -26.5) * mm, "end": v(6.77, -26.66) * mm});
            skLineSegment(sketch, "E355", {"start": v(6.77, -26.66) * mm, "end": v(6.34, -26.93) * mm});
            skLineSegment(sketch, "E356", {"start": v(6.34, -26.93) * mm, "end": v(5.98, -27.3) * mm});
            skLineSegment(sketch, "E357", {"start": v(5.98, -27.3) * mm, "end": v(5.67, -27.77) * mm});
            skLineSegment(sketch, "E358", {"start": v(5.67, -27.77) * mm, "end": v(5.47, -28.3) * mm});
            skLineSegment(sketch, "E359", {"start": v(5.47, -28.3) * mm, "end": v(5.35, -28.85) * mm});
            skLineSegment(sketch, "E360", {"start": v(5.35, -28.85) * mm, "end": v(5.32, -29.42) * mm});
            skLineSegment(sketch, "E361", {"start": v(2.97, -29.42) * mm, "end": v(2.98, -28.93) * mm});
            skLineSegment(sketch, "E362", {"start": v(2.98, -28.93) * mm, "end": v(3.03, -28.44) * mm});
            skLineSegment(sketch, "E363", {"start": v(3.03, -28.44) * mm, "end": v(3.13, -27.96) * mm});
            skLineSegment(sketch, "E364", {"start": v(3.13, -27.96) * mm, "end": v(3.26, -27.48) * mm});
            skLineSegment(sketch, "E365", {"start": v(3.26, -27.48) * mm, "end": v(3.44, -27.03) * mm});
            skLineSegment(sketch, "E366", {"start": v(3.44, -27.03) * mm, "end": v(3.67, -26.59) * mm});
            skLineSegment(sketch, "E367", {"start": v(3.67, -26.59) * mm, "end": v(3.94, -26.18) * mm});
            skLineSegment(sketch, "E368", {"start": v(3.94, -26.18) * mm, "end": v(4.25, -25.8) * mm});
            skLineSegment(sketch, "E369", {"start": v(4.25, -25.8) * mm, "end": v(4.6, -25.45) * mm});
            skLineSegment(sketch, "E370", {"start": v(4.6, -25.45) * mm, "end": v(4.98, -25.15) * mm});
            skLineSegment(sketch, "E371", {"start": v(4.98, -25.15) * mm, "end": v(5.4, -24.9) * mm});
            skLineSegment(sketch, "E372", {"start": v(5.4, -24.9) * mm, "end": v(5.85, -24.7) * mm});
            skLineSegment(sketch, "E373", {"start": v(5.85, -24.7) * mm, "end": v(6.32, -24.54) * mm});
            skLineSegment(sketch, "E374", {"start": v(6.32, -24.54) * mm, "end": v(6.8, -24.44) * mm});
            skLineSegment(sketch, "E375", {"start": v(6.8, -24.44) * mm, "end": v(7.28, -24.38) * mm});
            skLineSegment(sketch, "E376", {"start": v(7.28, -24.38) * mm, "end": v(7.77, -24.37) * mm});
            skLineSegment(sketch, "E377", {"start": v(7.77, -24.37) * mm, "end": v(8.27, -24.38) * mm});
            skLineSegment(sketch, "E378", {"start": v(8.27, -24.38) * mm, "end": v(8.75, -24.44) * mm});
            skLineSegment(sketch, "E379", {"start": v(8.75, -24.44) * mm, "end": v(9.23, -24.54) * mm});
            skLineSegment(sketch, "E380", {"start": v(9.23, -24.54) * mm, "end": v(9.7, -24.7) * mm});
            skLineSegment(sketch, "E381", {"start": v(9.7, -24.7) * mm, "end": v(10.15, -24.9) * mm});
            skLineSegment(sketch, "E382", {"start": v(10.15, -24.9) * mm, "end": v(10.57, -25.15) * mm});
            skLineSegment(sketch, "E383", {"start": v(10.57, -25.15) * mm, "end": v(10.96, -25.45) * mm});
            skLineSegment(sketch, "E384", {"start": v(10.96, -25.45) * mm, "end": v(11.3, -25.8) * mm});
            skLineSegment(sketch, "E385", {"start": v(11.3, -25.8) * mm, "end": v(11.61, -26.18) * mm});
            skLineSegment(sketch, "E386", {"start": v(11.61, -26.18) * mm, "end": v(11.88, -26.59) * mm});
            skLineSegment(sketch, "E387", {"start": v(11.88, -26.59) * mm, "end": v(12.1, -27.03) * mm});
            skLineSegment(sketch, "E388", {"start": v(12.1, -27.03) * mm, "end": v(12.29, -27.48) * mm});
            skLineSegment(sketch, "E389", {"start": v(12.29, -27.48) * mm, "end": v(12.42, -27.96) * mm});
            skLineSegment(sketch, "E390", {"start": v(12.42, -27.96) * mm, "end": v(12.51, -28.44) * mm});
            skLineSegment(sketch, "E391", {"start": v(12.51, -28.44) * mm, "end": v(12.57, -28.93) * mm});
            skLineSegment(sketch, "E392", {"start": v(12.57, -28.93) * mm, "end": v(12.59, -29.42) * mm});
            skLineSegment(sketch, "E393", {"start": v(12.59, -29.42) * mm, "end": v(12.57, -29.91) * mm});
            skLineSegment(sketch, "E394", {"start": v(12.57, -29.91) * mm, "end": v(12.51, -30.4) * mm});
            skLineSegment(sketch, "E395", {"start": v(12.51, -30.4) * mm, "end": v(12.42, -30.88) * mm});
            skLineSegment(sketch, "E396", {"start": v(12.42, -30.88) * mm, "end": v(12.29, -31.36) * mm});
            skLineSegment(sketch, "E397", {"start": v(12.29, -31.36) * mm, "end": v(12.1, -31.81) * mm});
            skLineSegment(sketch, "E398", {"start": v(12.1, -31.81) * mm, "end": v(11.88, -32.25) * mm});
            skLineSegment(sketch, "E399", {"start": v(11.88, -32.25) * mm, "end": v(11.61, -32.66) * mm});
            skLineSegment(sketch, "E400", {"start": v(11.61, -32.66) * mm, "end": v(11.3, -33.04) * mm});
            skLineSegment(sketch, "E401", {"start": v(11.3, -33.04) * mm, "end": v(10.96, -33.4) * mm});
            skLineSegment(sketch, "E402", {"start": v(10.96, -33.4) * mm, "end": v(10.57, -33.7) * mm});
            skLineSegment(sketch, "E403", {"start": v(10.57, -33.7) * mm, "end": v(10.15, -33.95) * mm});
            skLineSegment(sketch, "E404", {"start": v(10.15, -33.95) * mm, "end": v(9.7, -34.15) * mm});
            skLineSegment(sketch, "E405", {"start": v(9.7, -34.15) * mm, "end": v(9.23, -34.3) * mm});
            skLineSegment(sketch, "E406", {"start": v(9.23, -34.3) * mm, "end": v(8.75, -34.4) * mm});
            skLineSegment(sketch, "E407", {"start": v(8.75, -34.4) * mm, "end": v(8.27, -34.46) * mm});
            skLineSegment(sketch, "E408", {"start": v(8.27, -34.46) * mm, "end": v(7.77, -34.47) * mm});
            skLineSegment(sketch, "E409", {"start": v(7.77, -34.47) * mm, "end": v(7.28, -34.46) * mm});
            skLineSegment(sketch, "E410", {"start": v(7.28, -34.46) * mm, "end": v(6.8, -34.4) * mm});
            skLineSegment(sketch, "E411", {"start": v(6.8, -34.4) * mm, "end": v(6.32, -34.3) * mm});
            skLineSegment(sketch, "E412", {"start": v(6.32, -34.3) * mm, "end": v(5.85, -34.15) * mm});
            skLineSegment(sketch, "E413", {"start": v(5.85, -34.15) * mm, "end": v(5.4, -33.95) * mm});
            skLineSegment(sketch, "E414", {"start": v(5.4, -33.95) * mm, "end": v(4.98, -33.7) * mm});
            skLineSegment(sketch, "E415", {"start": v(4.98, -33.7) * mm, "end": v(4.6, -33.4) * mm});
            skLineSegment(sketch, "E416", {"start": v(4.6, -33.4) * mm, "end": v(4.25, -33.04) * mm});
            skLineSegment(sketch, "E417", {"start": v(4.25, -33.04) * mm, "end": v(3.94, -32.66) * mm});
            skLineSegment(sketch, "E418", {"start": v(3.94, -32.66) * mm, "end": v(3.67, -32.25) * mm});
            skLineSegment(sketch, "E419", {"start": v(3.67, -32.25) * mm, "end": v(3.44, -31.81) * mm});
            skLineSegment(sketch, "E420", {"start": v(3.44, -31.81) * mm, "end": v(3.26, -31.36) * mm});
            skLineSegment(sketch, "E421", {"start": v(3.26, -31.36) * mm, "end": v(3.13, -30.88) * mm});
            skLineSegment(sketch, "E422", {"start": v(3.13, -30.88) * mm, "end": v(3.03, -30.4) * mm});
            skLineSegment(sketch, "E423", {"start": v(3.03, -30.4) * mm, "end": v(2.98, -29.91) * mm});
            skLineSegment(sketch, "E424", {"start": v(2.98, -29.91) * mm, "end": v(2.97, -29.42) * mm});
            skLineSegment(sketch, "E425", {"start": v(17.97, -32.2) * mm, "end": v(18.13, -32.2) * mm});
            skLineSegment(sketch, "E426", {"start": v(18.13, -32.2) * mm, "end": v(18.52, -32.2) * mm});
            skLineSegment(sketch, "E427", {"start": v(18.52, -32.2) * mm, "end": v(19.08, -32.2) * mm});
            skLineSegment(sketch, "E428", {"start": v(19.08, -32.2) * mm, "end": v(19.63, -32.2) * mm});
            skLineSegment(sketch, "E429", {"start": v(19.63, -32.2) * mm, "end": v(20.02, -32.2) * mm});
            skLineSegment(sketch, "E430", {"start": v(20.02, -32.2) * mm, "end": v(20.18, -32.2) * mm});
            skLineSegment(sketch, "E431", {"start": v(20.18, -32.2) * mm, "end": v(20.18, -32.73) * mm});
            skLineSegment(sketch, "E432", {"start": v(20.18, -32.73) * mm, "end": v(20.18, -33.25) * mm});
            skLineSegment(sketch, "E433", {"start": v(20.18, -33.25) * mm, "end": v(20.18, -33.78) * mm});
            skLineSegment(sketch, "E434", {"start": v(20.18, -33.78) * mm, "end": v(20.18, -34.3) * mm});
            skLineSegment(sketch, "E435", {"start": v(20.18, -34.3) * mm, "end": v(19.63, -34.3) * mm});
            skLineSegment(sketch, "E436", {"start": v(19.63, -34.3) * mm, "end": v(19.07, -34.3) * mm});
            skLineSegment(sketch, "E437", {"start": v(19.07, -34.3) * mm, "end": v(18.52, -34.3) * mm});
            skLineSegment(sketch, "E438", {"start": v(18.52, -34.3) * mm, "end": v(17.96, -34.3) * mm});
            skLineSegment(sketch, "E439", {"start": v(17.96, -34.3) * mm, "end": v(17.4, -34.3) * mm});
            skLineSegment(sketch, "E440", {"start": v(17.4, -34.3) * mm, "end": v(16.85, -34.3) * mm});
            skLineSegment(sketch, "E441", {"start": v(16.85, -34.3) * mm, "end": v(16.3, -34.3) * mm});
            skLineSegment(sketch, "E442", {"start": v(16.3, -34.3) * mm, "end": v(15.75, -34.3) * mm});
            skLineSegment(sketch, "E443", {"start": v(15.75, -34.3) * mm, "end": v(15.19, -34.3) * mm});
            skLineSegment(sketch, "E444", {"start": v(15.19, -34.3) * mm, "end": v(14.64, -34.3) * mm});
            skLineSegment(sketch, "E445", {"start": v(14.64, -34.3) * mm, "end": v(14.08, -34.3) * mm});
            skLineSegment(sketch, "E446", {"start": v(14.08, -34.3) * mm, "end": v(13.53, -34.3) * mm});
            skLineSegment(sketch, "E447", {"start": v(13.53, -34.3) * mm, "end": v(13.53, -33.78) * mm});
            skLineSegment(sketch, "E448", {"start": v(13.53, -33.78) * mm, "end": v(13.53, -33.25) * mm});
            skLineSegment(sketch, "E449", {"start": v(13.53, -33.25) * mm, "end": v(13.53, -32.73) * mm});
            skLineSegment(sketch, "E450", {"start": v(13.53, -32.73) * mm, "end": v(13.53, -32.2) * mm});
            skLineSegment(sketch, "E451", {"start": v(13.53, -32.2) * mm, "end": v(14.07, -32.2) * mm});
            skLineSegment(sketch, "E452", {"start": v(14.07, -32.2) * mm, "end": v(14.62, -32.2) * mm});
            skLineSegment(sketch, "E453", {"start": v(14.62, -32.2) * mm, "end": v(15.16, -32.2) * mm});
            skLineSegment(sketch, "E454", {"start": v(15.16, -32.2) * mm, "end": v(15.7, -32.2) * mm});
            skLineSegment(sketch, "E455", {"start": v(15.7, -32.2) * mm, "end": v(15.7, -32.04) * mm});
            skLineSegment(sketch, "E456", {"start": v(15.7, -32.04) * mm, "end": v(15.7, -31.59) * mm});
            skLineSegment(sketch, "E457", {"start": v(15.7, -31.59) * mm, "end": v(15.7, -30.96) * mm});
            skLineSegment(sketch, "E458", {"start": v(15.7, -30.96) * mm, "end": v(15.7, -30.34) * mm});
            skLineSegment(sketch, "E459", {"start": v(15.7, -30.34) * mm, "end": v(15.7, -29.72) * mm});
            skLineSegment(sketch, "E460", {"start": v(15.7, -29.72) * mm, "end": v(15.7, -29.1) * mm});
            skLineSegment(sketch, "E461", {"start": v(15.7, -29.1) * mm, "end": v(15.7, -28.47) * mm});
            skLineSegment(sketch, "E462", {"start": v(15.7, -28.47) * mm, "end": v(15.7, -27.85) * mm});
            skLineSegment(sketch, "E463", {"start": v(15.7, -27.85) * mm, "end": v(15.7, -27.4) * mm});
            skLineSegment(sketch, "E464", {"start": v(15.7, -27.4) * mm, "end": v(15.7, -27.22) * mm});
            skLineSegment(sketch, "E465", {"start": v(15.7, -27.22) * mm, "end": v(15.57, -27.25) * mm});
            skLineSegment(sketch, "E466", {"start": v(15.57, -27.25) * mm, "end": v(15.23, -27.32) * mm});
            skLineSegment(sketch, "E467", {"start": v(15.23, -27.32) * mm, "end": v(14.75, -27.42) * mm});
            skLineSegment(sketch, "E468", {"start": v(14.75, -27.42) * mm, "end": v(14.27, -27.52) * mm});
            skLineSegment(sketch, "E469", {"start": v(14.27, -27.52) * mm, "end": v(13.92, -27.6) * mm});
            skLineSegment(sketch, "E470", {"start": v(13.92, -27.6) * mm, "end": v(13.79, -27.62) * mm});
            skLineSegment(sketch, "E471", {"start": v(13.79, -27.62) * mm, "end": v(13.72, -27.37) * mm});
            skLineSegment(sketch, "E472", {"start": v(13.72, -27.37) * mm, "end": v(13.56, -26.82) * mm});
            skLineSegment(sketch, "E473", {"start": v(13.56, -26.82) * mm, "end": v(13.4, -26.27) * mm});
            skLineSegment(sketch, "E474", {"start": v(13.4, -26.27) * mm, "end": v(13.33, -26.02) * mm});
            skLineSegment(sketch, "E475", {"start": v(13.33, -26.02) * mm, "end": v(13.5, -25.96) * mm});
            skLineSegment(sketch, "E476", {"start": v(13.5, -25.96) * mm, "end": v(13.91, -25.81) * mm});
            skLineSegment(sketch, "E477", {"start": v(13.91, -25.81) * mm, "end": v(14.5, -25.6) * mm});
            skLineSegment(sketch, "E478", {"start": v(14.5, -25.6) * mm, "end": v(15.07, -25.4) * mm});
            skLineSegment(sketch, "E479", {"start": v(15.07, -25.4) * mm, "end": v(15.65, -25.2) * mm});
            skLineSegment(sketch, "E480", {"start": v(15.65, -25.2) * mm, "end": v(16.23, -24.99) * mm});
            skLineSegment(sketch, "E481", {"start": v(16.23, -24.99) * mm, "end": v(16.81, -24.78) * mm});
            skLineSegment(sketch, "E482", {"start": v(16.81, -24.78) * mm, "end": v(17.4, -24.57) * mm});
            skLineSegment(sketch, "E483", {"start": v(17.4, -24.57) * mm, "end": v(17.81, -24.42) * mm});
            skLineSegment(sketch, "E484", {"start": v(17.81, -24.42) * mm, "end": v(17.97, -24.37) * mm});
            skLineSegment(sketch, "E485", {"start": v(17.97, -24.37) * mm, "end": v(17.97, -24.54) * mm});
            skLineSegment(sketch, "E486", {"start": v(17.97, -24.54) * mm, "end": v(17.97, -25.02) * mm});
            skLineSegment(sketch, "E487", {"start": v(17.97, -25.02) * mm, "end": v(17.97, -25.67) * mm});
            skLineSegment(sketch, "E488", {"start": v(17.97, -25.67) * mm, "end": v(17.97, -26.33) * mm});
            skLineSegment(sketch, "E489", {"start": v(17.97, -26.33) * mm, "end": v(17.97, -26.98) * mm});
            skLineSegment(sketch, "E490", {"start": v(17.97, -26.98) * mm, "end": v(17.97, -27.63) * mm});
            skLineSegment(sketch, "E491", {"start": v(17.97, -27.63) * mm, "end": v(17.97, -28.29) * mm});
            skLineSegment(sketch, "E492", {"start": v(17.97, -28.29) * mm, "end": v(17.97, -28.94) * mm});
            skLineSegment(sketch, "E493", {"start": v(17.97, -28.94) * mm, "end": v(17.97, -29.6) * mm});
            skLineSegment(sketch, "E494", {"start": v(17.97, -29.6) * mm, "end": v(17.97, -30.25) * mm});
            skLineSegment(sketch, "E495", {"start": v(17.97, -30.25) * mm, "end": v(17.97, -30.9) * mm});
            skLineSegment(sketch, "E496", {"start": v(17.97, -30.9) * mm, "end": v(17.97, -31.55) * mm});
            skLineSegment(sketch, "E497", {"start": v(17.97, -31.55) * mm, "end": v(17.97, -32.03) * mm});
            skLineSegment(sketch, "E498", {"start": v(17.97, -32.03) * mm, "end": v(17.97, -32.2) * mm});
            skLineSegment(sketch, "E499", {"start": v(24.89, -37.26) * mm, "end": v(24.34, -37.26) * mm});
            skLineSegment(sketch, "E500", {"start": v(24.34, -37.26) * mm, "end": v(23.8, -37.26) * mm});
            skLineSegment(sketch, "E501", {"start": v(23.8, -37.26) * mm, "end": v(23.26, -37.26) * mm});
            skLineSegment(sketch, "E502", {"start": v(23.26, -37.26) * mm, "end": v(22.7, -37.26) * mm});
            skLineSegment(sketch, "E503", {"start": v(22.7, -37.26) * mm, "end": v(22.74, -36.49) * mm});
            skLineSegment(sketch, "E504", {"start": v(22.74, -36.49) * mm, "end": v(22.82, -35.72) * mm});
            skLineSegment(sketch, "E505", {"start": v(22.82, -35.72) * mm, "end": v(22.95, -34.96) * mm});
            skLineSegment(sketch, "E506", {"start": v(22.95, -34.96) * mm, "end": v(23.13, -34.21) * mm});
            skLineSegment(sketch, "E507", {"start": v(23.13, -34.21) * mm, "end": v(23.32, -33.54) * mm});
            skLineSegment(sketch, "E508", {"start": v(23.32, -33.54) * mm, "end": v(23.54, -32.88) * mm});
            skLineSegment(sketch, "E509", {"start": v(23.54, -32.88) * mm, "end": v(23.8, -32.23) * mm});
            skLineSegment(sketch, "E510", {"start": v(23.8, -32.23) * mm, "end": v(24.08, -31.6) * mm});
            skLineSegment(sketch, "E511", {"start": v(24.08, -31.6) * mm, "end": v(24.39, -30.97) * mm});
            skLineSegment(sketch, "E512", {"start": v(24.39, -30.97) * mm, "end": v(24.7, -30.34) * mm});
            skLineSegment(sketch, "E513", {"start": v(24.7, -30.34) * mm, "end": v(25, -29.7) * mm});
            skLineSegment(sketch, "E514", {"start": v(25, -29.7) * mm, "end": v(25.3, -29.08) * mm});
            skLineSegment(sketch, "E515", {"start": v(25.3, -29.08) * mm, "end": v(25.59, -28.48) * mm});
            skLineSegment(sketch, "E516", {"start": v(25.59, -28.48) * mm, "end": v(25.86, -27.88) * mm});
            skLineSegment(sketch, "E517", {"start": v(25.86, -27.88) * mm, "end": v(26.12, -27.27) * mm});
            skLineSegment(sketch, "E518", {"start": v(26.12, -27.27) * mm, "end": v(26.35, -26.65) * mm});
            skLineSegment(sketch, "E519", {"start": v(26.35, -26.65) * mm, "end": v(25.91, -26.65) * mm});
            skLineSegment(sketch, "E520", {"start": v(25.91, -26.65) * mm, "end": v(25.47, -26.65) * mm});
            skLineSegment(sketch, "E521", {"start": v(25.47, -26.65) * mm, "end": v(25.03, -26.65) * mm});
            skLineSegment(sketch, "E522", {"start": v(25.03, -26.65) * mm, "end": v(24.6, -26.65) * mm});
            skLineSegment(sketch, "E523", {"start": v(24.6, -26.65) * mm, "end": v(24.15, -26.65) * mm});
            skLineSegment(sketch, "E524", {"start": v(24.15, -26.65) * mm, "end": v(23.71, -26.65) * mm});
            skLineSegment(sketch, "E525", {"start": v(23.71, -26.65) * mm, "end": v(23.27, -26.65) * mm});
            skLineSegment(sketch, "E526", {"start": v(23.27, -26.65) * mm, "end": v(22.83, -26.65) * mm});
            skLineSegment(sketch, "E527", {"start": v(22.83, -26.65) * mm, "end": v(22.83, -26.86) * mm});
            skLineSegment(sketch, "E528", {"start": v(22.83, -26.86) * mm, "end": v(22.83, -27.34) * mm});
            skLineSegment(sketch, "E529", {"start": v(22.83, -27.34) * mm, "end": v(22.83, -27.8) * mm});
            skLineSegment(sketch, "E530", {"start": v(22.83, -27.8) * mm, "end": v(22.83, -28.03) * mm});
            skLineSegment(sketch, "E531", {"start": v(22.83, -28.03) * mm, "end": v(22.33, -28.03) * mm});
            skLineSegment(sketch, "E532", {"start": v(22.33, -28.03) * mm, "end": v(21.83, -28.03) * mm});
            skLineSegment(sketch, "E533", {"start": v(21.83, -28.03) * mm, "end": v(21.33, -28.03) * mm});
            skLineSegment(sketch, "E534", {"start": v(21.33, -28.03) * mm, "end": v(20.83, -28.03) * mm});
            skLineSegment(sketch, "E535", {"start": v(20.83, -28.03) * mm, "end": v(20.83, -27.78) * mm});
            skLineSegment(sketch, "E536", {"start": v(20.83, -27.78) * mm, "end": v(20.83, -27.16) * mm});
            skLineSegment(sketch, "E537", {"start": v(20.83, -27.16) * mm, "end": v(20.83, -26.3) * mm});
            skLineSegment(sketch, "E538", {"start": v(20.83, -26.3) * mm, "end": v(20.83, -25.42) * mm});
            skLineSegment(sketch, "E539", {"start": v(20.83, -25.42) * mm, "end": v(20.83, -24.8) * mm});
            skLineSegment(sketch, "E540", {"start": v(20.83, -24.8) * mm, "end": v(20.83, -24.56) * mm});
            skLineSegment(sketch, "E541", {"start": v(20.83, -24.56) * mm, "end": v(21, -24.56) * mm});
            skLineSegment(sketch, "E542", {"start": v(21, -24.56) * mm, "end": v(21.47, -24.56) * mm});
            skLineSegment(sketch, "E543", {"start": v(21.47, -24.56) * mm, "end": v(22.11, -24.56) * mm});
            skLineSegment(sketch, "E544", {"start": v(22.11, -24.56) * mm, "end": v(22.75, -24.56) * mm});
            skLineSegment(sketch, "E545", {"start": v(22.75, -24.56) * mm, "end": v(23.4, -24.56) * mm});
            skLineSegment(sketch, "E546", {"start": v(23.4, -24.56) * mm, "end": v(24.04, -24.56) * mm});
            skLineSegment(sketch, "E547", {"start": v(24.04, -24.56) * mm, "end": v(24.68, -24.56) * mm});
            skLineSegment(sketch, "E548", {"start": v(24.68, -24.56) * mm, "end": v(25.32, -24.56) * mm});
            skLineSegment(sketch, "E549", {"start": v(25.32, -24.56) * mm, "end": v(25.96, -24.56) * mm});
            skLineSegment(sketch, "E550", {"start": v(25.96, -24.56) * mm, "end": v(26.6, -24.56) * mm});
            skLineSegment(sketch, "E551", {"start": v(26.6, -24.56) * mm, "end": v(27.25, -24.56) * mm});
            skLineSegment(sketch, "E552", {"start": v(27.25, -24.56) * mm, "end": v(27.89, -24.56) * mm});
            skLineSegment(sketch, "E553", {"start": v(27.89, -24.56) * mm, "end": v(28.36, -24.56) * mm});
            skLineSegment(sketch, "E554", {"start": v(28.36, -24.56) * mm, "end": v(28.53, -24.56) * mm});
            skLineSegment(sketch, "E555", {"start": v(28.53, -24.56) * mm, "end": v(28.53, -25.08) * mm});
            skLineSegment(sketch, "E556", {"start": v(28.53, -25.08) * mm, "end": v(28.53, -25.6) * mm});
            skLineSegment(sketch, "E557", {"start": v(28.53, -25.6) * mm, "end": v(28.53, -26.11) * mm});
            skLineSegment(sketch, "E558", {"start": v(28.53, -26.11) * mm, "end": v(28.53, -26.63) * mm});
            skLineSegment(sketch, "E559", {"start": v(28.53, -26.63) * mm, "end": v(28.48, -27.1) * mm});
            skLineSegment(sketch, "E560", {"start": v(28.48, -27.1) * mm, "end": v(28.37, -27.54) * mm});
            skLineSegment(sketch, "E561", {"start": v(28.37, -27.54) * mm, "end": v(28.22, -27.98) * mm});
            skLineSegment(sketch, "E562", {"start": v(28.22, -27.98) * mm, "end": v(28.05, -28.41) * mm});
            skLineSegment(sketch, "E563", {"start": v(28.05, -28.41) * mm, "end": v(27.86, -28.84) * mm});
            skLineSegment(sketch, "E564", {"start": v(27.86, -28.84) * mm, "end": v(27.67, -29.26) * mm});
            skLineSegment(sketch, "E565", {"start": v(27.67, -29.26) * mm, "end": v(27.46, -29.67) * mm});
            skLineSegment(sketch, "E566", {"start": v(27.46, -29.67) * mm, "end": v(27.24, -30.08) * mm});
            skLineSegment(sketch, "E567", {"start": v(27.24, -30.08) * mm, "end": v(26.96, -30.6) * mm});
            skLineSegment(sketch, "E568", {"start": v(26.96, -30.6) * mm, "end": v(26.7, -31.12) * mm});
            skLineSegment(sketch, "E569", {"start": v(26.7, -31.12) * mm, "end": v(26.43, -31.65) * mm});
            skLineSegment(sketch, "E570", {"start": v(26.43, -31.65) * mm, "end": v(26.17, -32.17) * mm});
            skLineSegment(sketch, "E571", {"start": v(26.17, -32.17) * mm, "end": v(25.9, -32.77) * mm});
            skLineSegment(sketch, "E572", {"start": v(25.9, -32.77) * mm, "end": v(25.66, -33.38) * mm});
            skLineSegment(sketch, "E573", {"start": v(25.66, -33.38) * mm, "end": v(25.45, -34) * mm});
            skLineSegment(sketch, "E574", {"start": v(25.45, -34) * mm, "end": v(25.26, -34.62) * mm});
            skLineSegment(sketch, "E575", {"start": v(25.26, -34.62) * mm, "end": v(25.1, -35.27) * mm});
            skLineSegment(sketch, "E576", {"start": v(25.1, -35.27) * mm, "end": v(24.99, -35.93) * mm});
            skLineSegment(sketch, "E577", {"start": v(24.99, -35.93) * mm, "end": v(24.91, -36.6) * mm});
            skLineSegment(sketch, "E578", {"start": v(24.91, -36.6) * mm, "end": v(24.89, -37.26) * mm});
            skSolve(sketch);
        }
        {
            var Q0;
            Q0 = qSketchRegion(id + "F2", true);
            extrude(context, id + "F3", {"entities" : qUnion([Q0]), "depth" : 3 * mm});
        }
    });
